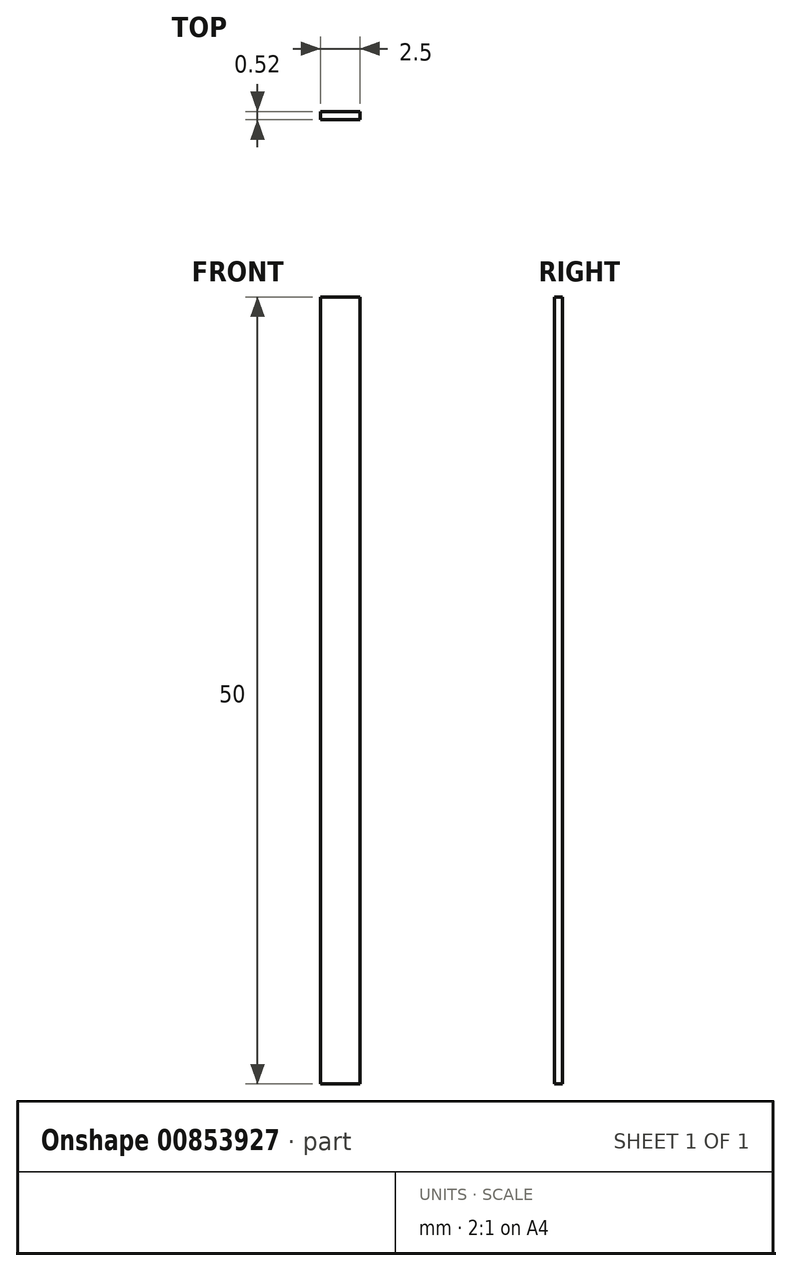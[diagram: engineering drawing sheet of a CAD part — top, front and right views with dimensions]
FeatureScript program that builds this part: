
annotation { "Feature Type Name" : "Feature", "Feature Type Description" : "" }
export const myFeature = defineFeature(function(context is Context, id is Id, definition is map)
    precondition{}
    {
        {
            var Q0;
            Q0=qCreatedBy(makeId("Top.planeOp"),FACE);
            var sketch = newSketch(context, id + "F0", { "sketchPlane" : qUnion([Q0])});
            skLineSegment(sketch, "E0", {"start": v(12.08, 0) * mm, "end": v(22.08, 0) * mm});
            skLineSegment(sketch, "E1", {"start": v(22.08, 0) * mm, "end": v(23.66, 4.74) * mm});
            skFitSpline(sketch, "E2", {"points": [v(-18.22, 0) * mm, v(0, 26.21) * mm, v(12.08, 0) * mm], "startDerivative": vector(76.65, 126.29) * mm, "endDerivative": vector(47.78, -124.15) * mm});
            skLineSegment(sketch, "E3.0", {"start": v(21.36, 1) * mm, "end": v(22.72, 5.06) * mm});
            skLineSegment(sketch, "E3.1", {"start": v(12.77, 1) * mm, "end": v(21.36, 1) * mm});
            skFitSpline(sketch, "E3.2", {"points": [v(-19.07, 0.52) * mm, v(-17.47, 3.15) * mm, v(-14.6, 7.92) * mm, v(-11.08, 13.73) * mm, v(-8.27, 18.32) * mm, v(-6.05, 21.8) * mm, v(-4.6, 23.9) * mm, v(-3.6, 25.16) * mm, v(-2.9, 25.92) * mm, v(-2.24, 26.51) * mm, v(-1.57, 26.95) * mm, v(-0.85, 27.22) * mm, v(-0.2, 27.26) * mm, v(0.27, 27.18) * mm, v(0.74, 27.04) * mm, v(1.29, 26.74) * mm, v(1.87, 26.23) * mm, v(2.6, 25.36) * mm, v(3.5, 23.9) * mm, v(4.73, 21.36) * mm, v(6.2, 17.9) * mm, v(8, 13.36) * mm, v(10.22, 7.64) * mm, v(12.02, 2.95) * mm, v(13.01, 0.36) * mm]});
            skLineSegment(sketch, "E4", {"start": v(-19.07, 0.52) * mm, "end": v(-18.22, 0) * mm});
            skLineSegment(sketch, "E5", {"start": v(22.72, 5.06) * mm, "end": v(23.66, 4.74) * mm});
            skLineSegment(sketch, "E6.bottom", {"start": v(-19.07, 0.52) * mm, "end": v(-16.57, 0.52) * mm});
            skLineSegment(sketch, "E6.top", {"start": v(-19.07, 0) * mm, "end": v(-16.57, 0) * mm});
            skLineSegment(sketch, "E6.left", {"start": v(-19.07, 0.52) * mm, "end": v(-19.07, 0) * mm});
            skLineSegment(sketch, "E6.right", {"start": v(-16.57, 0.52) * mm, "end": v(-16.57, 0) * mm});
            skSolve(sketch);
        }
        {
            var Q0;
            Q0 = qSketchRegion(id + "F0", true);
            extrude(context, id + "F1", {"entities" : qUnion([Q0]), "depth" : 50 * mm, "offsetDistance" : 25 * mm});
        }
    });
